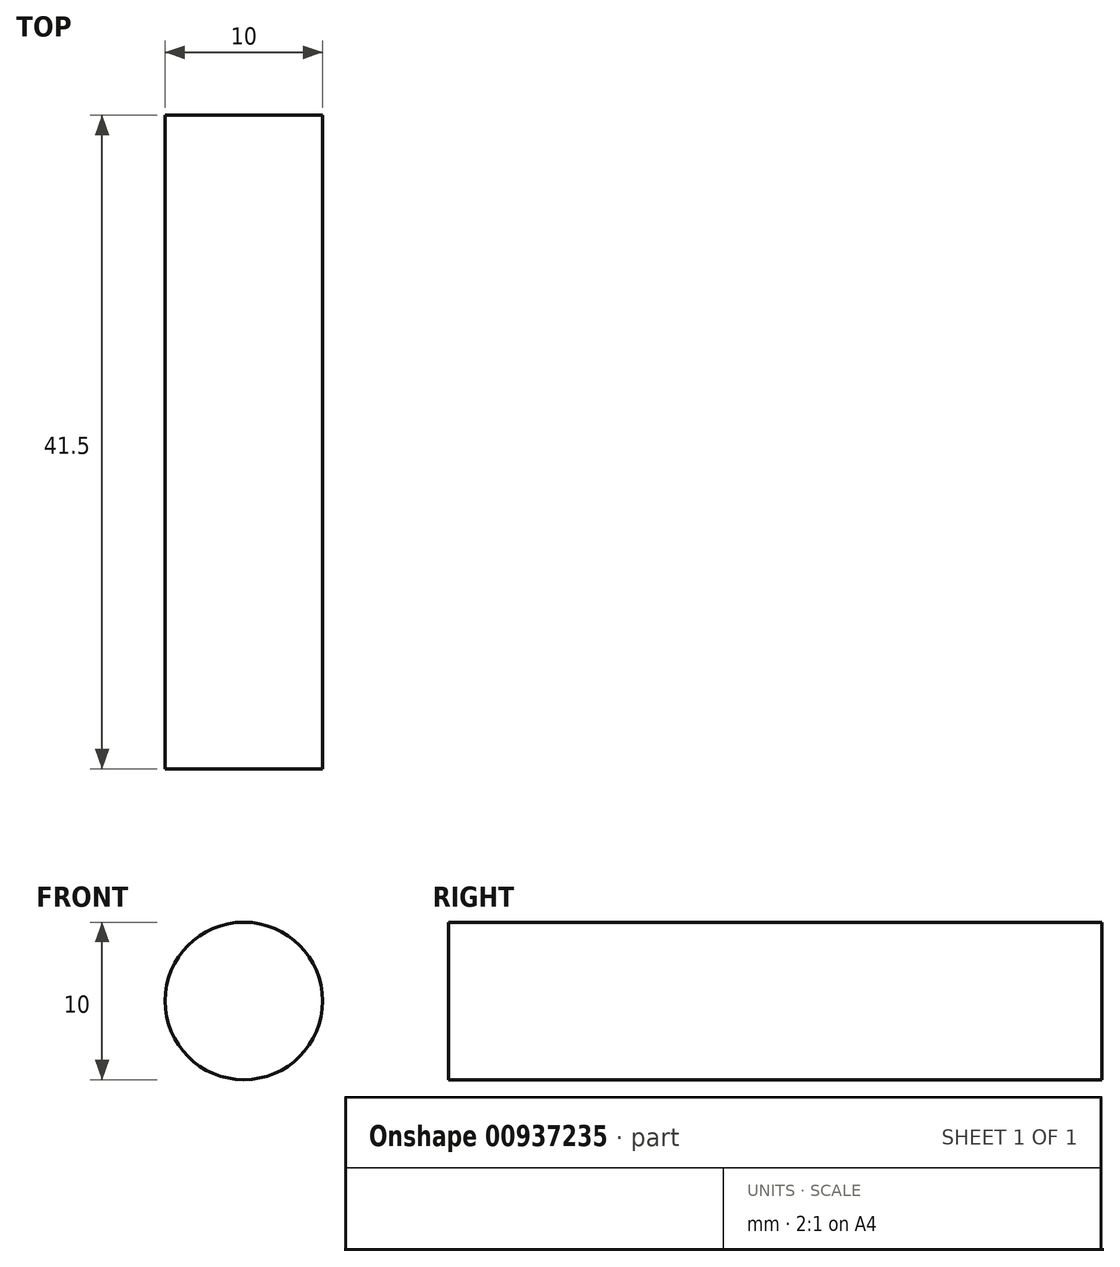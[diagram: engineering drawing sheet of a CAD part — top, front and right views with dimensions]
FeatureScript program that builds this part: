
annotation { "Feature Type Name" : "Feature", "Feature Type Description" : "" }
export const myFeature = defineFeature(function(context is Context, id is Id, definition is map)
    precondition{}
    {
        {
            var Q0;
            Q0=qCreatedBy(makeId("Front.planeOp"),FACE);
            var sketch = newSketch(context, id + "F0", { "sketchPlane" : qUnion([Q0])});
            skCircle(sketch, "E0", {"center": v(0, 0) * mm, "radius": 5 * mm});
            skSolve(sketch);
        }
        {
            var Q0;
            Q0=makeQuery(id+"F0.imprint","IMPRINT",FACE,{"disambiguationData":[TD([[makeQuery(id+"F0.imprint","IMPRINT",EDGE,{"derivedFrom":sQuery(id+"F0.wireOp",EDGE,"E0")}),1.0]])]});
            extrude(context, id + "F1", {"entities" : qUnion([Q0]), "oppositeDirection" : true, "depth" : 41.5 * mm, "offsetDistance" : 25 * mm, "symmetric" : true});
        }
    });
